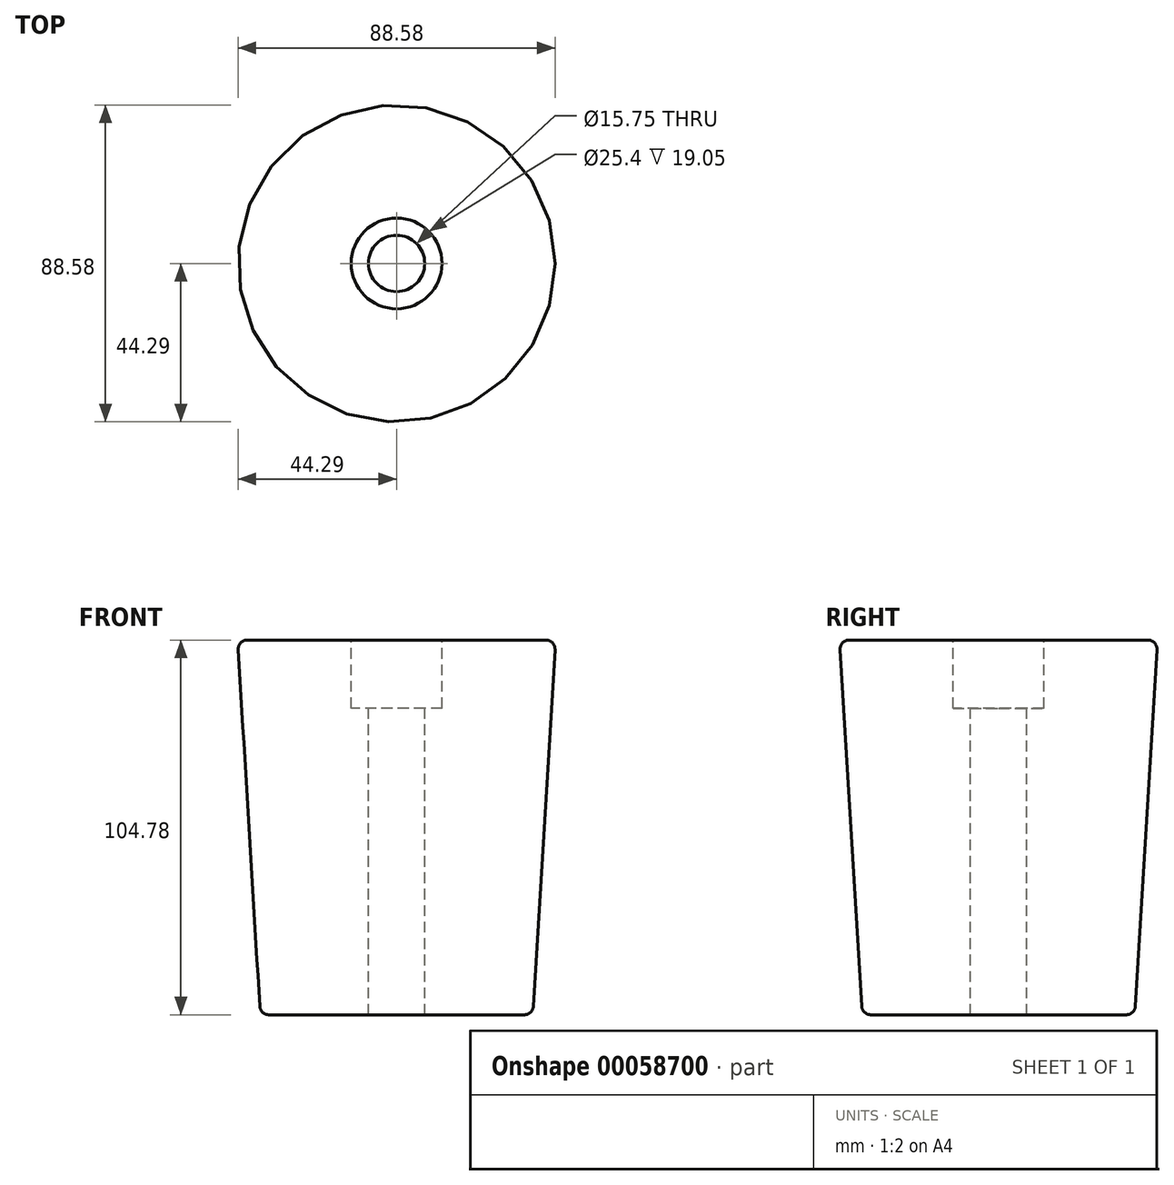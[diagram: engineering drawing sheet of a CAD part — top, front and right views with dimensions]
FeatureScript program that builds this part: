
annotation { "Feature Type Name" : "Feature", "Feature Type Description" : "" }
export const myFeature = defineFeature(function(context is Context, id is Id, definition is map)
    precondition{}
    {
        {
            var Q0;
            Q0=qCreatedBy(makeId("Front.planeOp"),FACE);
            var sketch = newSketch(context, id + "F0", { "sketchPlane" : qUnion([Q0])});
            skLineSegment(sketch, "E0", {"start": v(0, 63.5) * mm, "end": v(0, -63.5) * mm, "construction": true});
            skLineSegment(sketch, "E1", {"start": v(7.87, 63.5) * mm, "end": v(7.87, -63.5) * mm, "construction": true});
            skLineSegment(sketch, "E2", {"start": v(-63.5, 0) * mm, "end": v(63.5, 0) * mm, "construction": true});
            skLineSegment(sketch, "E3", {"start": v(7.87, 33.34) * mm, "end": v(12.7, 33.34) * mm});
            skLineSegment(sketch, "E4", {"start": v(12.7, 33.34) * mm, "end": v(12.7, 52.39) * mm});
            skLineSegment(sketch, "E5", {"start": v(12.7, 52.39) * mm, "end": v(44.45, 52.39) * mm});
            skLineSegment(sketch, "E6", {"start": v(44.45, 52.39) * mm, "end": v(38.1, -52.39) * mm});
            skLineSegment(sketch, "E7", {"start": v(38.1, -52.39) * mm, "end": v(7.87, -52.39) * mm});
            skLineSegment(sketch, "E8", {"start": v(7.87, -52.39) * mm, "end": v(7.87, 33.34) * mm});
            skSolve(sketch);
        }
        {
            var Q0;
            Q0=makeQuery(id+"F0.imprint","IMPRINT",FACE,{"disambiguationData":[TD([[makeQuery(id+"F0.imprint","IMPRINT",EDGE,{"derivedFrom":sQuery(id+"F0.wireOp",EDGE,"E3")}),-1.0]])]});
            var Q1;
            Q1=sQuery(id+"F0.wireOp",EDGE,"E0");
            revolve(context, id + "F1", {"entities" : qUnion([Q0]), "axis" : qUnion([Q1]), "revolveType" : RevolveType.FULL});
        }
        {
            var Q0;
            Q0=makeQuery(id+"F1.opRevolve","SWEPT_EDGE",EDGE,{"disambiguationData":[OSD([sQuery(id+"F0.wireOp",EDGE,"E5"),sQuery(id+"F0.wireOp",EDGE,"E6")])]});
            var Q1;
            Q1=makeQuery(id+"F1.opRevolve","SWEPT_EDGE",EDGE,{"disambiguationData":[OSD([sQuery(id+"F0.wireOp",EDGE,"E6"),sQuery(id+"F0.wireOp",EDGE,"E7")])]});
            fillet(context, id + "F2", {"entities" : qUnion([Q0, Q1]), "radius" : 2.54 * mm, "tangentPropagation" : true, "allowEdgeOverflow" : false});
        }
    });
